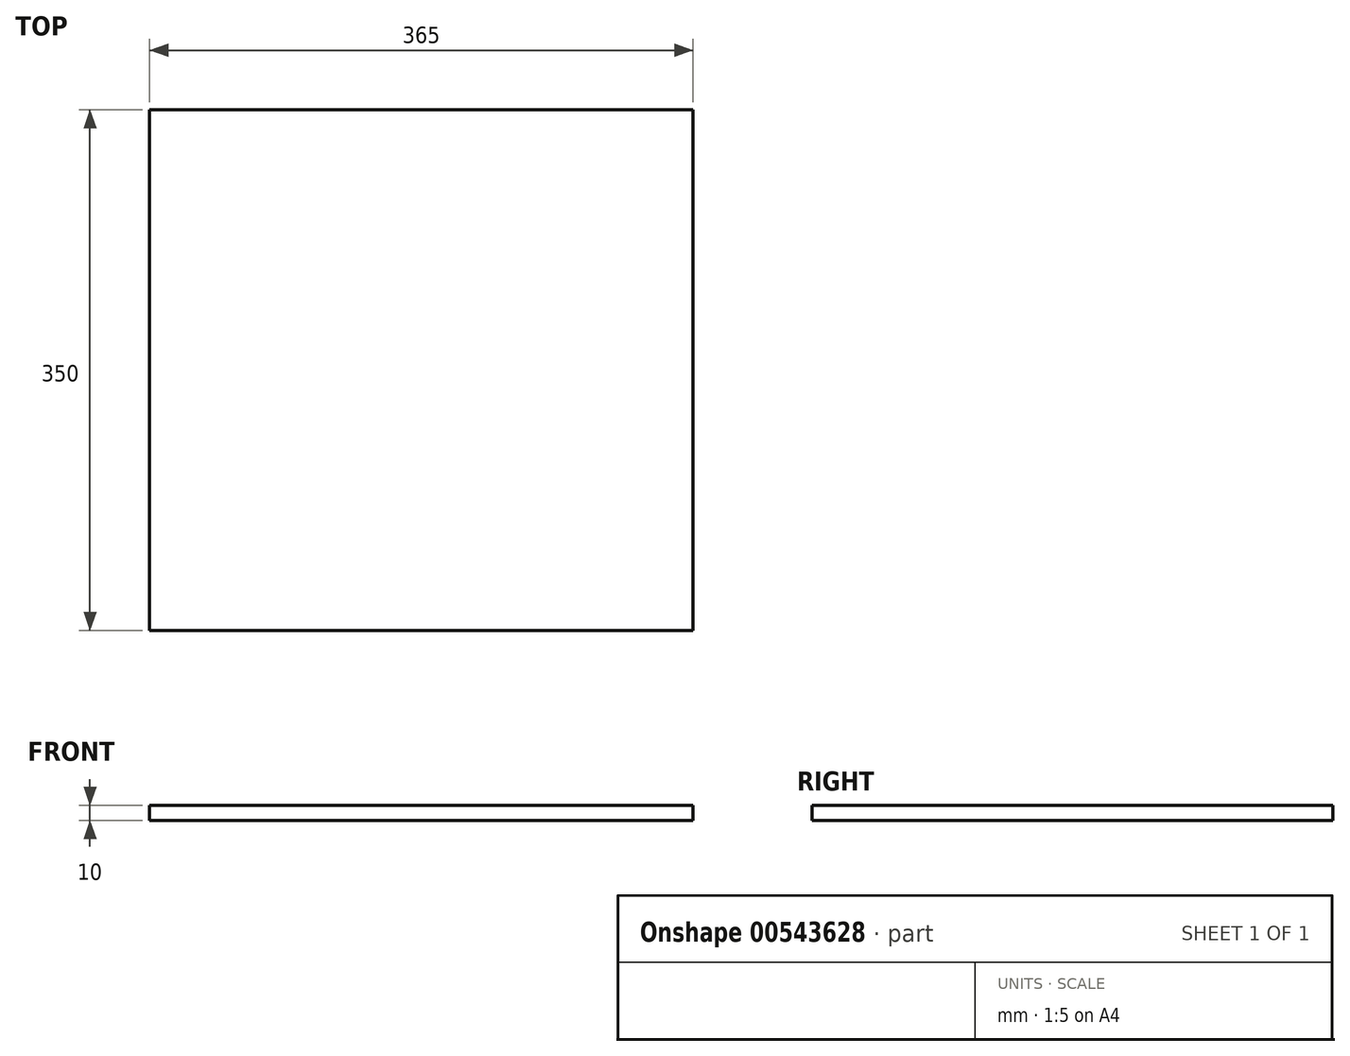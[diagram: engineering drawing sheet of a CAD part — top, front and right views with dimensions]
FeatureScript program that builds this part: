
annotation { "Feature Type Name" : "Feature", "Feature Type Description" : "" }
export const myFeature = defineFeature(function(context is Context, id is Id, definition is map)
    precondition{}
    {
        {
            var Q0;
            Q0=qCreatedBy(makeId("Top.planeOp"),FACE);
            var sketch = newSketch(context, id + "F0", { "sketchPlane" : qUnion([Q0])});
            skLineSegment(sketch, "E0.bottom", {"start": v(-70.96, 65.05) * mm, "end": v(294.04, 65.05) * mm});
            skLineSegment(sketch, "E0.top", {"start": v(-70.96, -284.95) * mm, "end": v(294.04, -284.95) * mm});
            skLineSegment(sketch, "E0.left", {"start": v(-70.96, 65.05) * mm, "end": v(-70.96, -284.95) * mm});
            skLineSegment(sketch, "E0.right", {"start": v(294.04, 65.05) * mm, "end": v(294.04, -284.95) * mm});
            skSolve(sketch);
        }
        {
            var Q0;
            Q0=qSketchRegion(id+"F0",true);
            extrude(context, id + "F1", {"entities" : qUnion([Q0]), "depth" : 10 * mm});
        }
    });
